# Revit family: Zurn_One-System-Zurn-Z.L6.S
name_source: partatom
category: Plumbing Fixtures
units: mm (PartAtom-declared; Revit-internal decimal feet)

## family parameters
Always vertical = Yes
Cut with Voids When Loaded = No
Maintain Annotation Orientation = No
OmniClass Number = 23.45.05.14
OmniClass Title = Plumbing Fixtures - Sanitary Washing Units
Part Type = Normal
Room Calculation Point = No
Round Connector Dimension = Use Radius
Shared = No
Work Plane-Based = No

## types (1)
- Z.L6.S (20” x 18” Wall Hung Lavatory Zurn One Sensor Hand Washing System)
    Activation Method = Sensor Activation
    Angle stop Location from Sink Top = 10 "
    Assembly Code = D2010
    CW Connection = Yes
    CWFU = 1
    Cold Water Inlet Connection Size (inch) = 0.5 "
    Default Elevation = 0 "
    Description = 20” x 18” Wall Hung Lavatory Zurn One Sensor Hand Washing System
    Distance B/w Angle Stop Body Location = 8 "
    Distance between Sink and Ground = 34 "
    Faucet Material = Chrome-Plated Brass - Zurn - Polished
    Faucet Number = ZG6915-XL
    Fixture Material = China - Zurn - Vitreous
    Fixture Number = Z5344
    Flow Rate (GPM) = 1 GPM
    HW Connection = Yes
    HWFU = 1
    Hot Water Inlet Connection Size (inch) = 0.5 "
    Length odf Sink = 18.25 "
    Manufacturer = Zurn
    Manufacturer Brand = Zurn Water, LLC
    Model = Z.L6.S
    Modified Date = 02/25/2026
    P-trap Hole Location = 12.75 "
    Product Documentation Link = https://files.zurn.com
    Product Page URL = https://www.zurn.com
    Product data URL = https://bimobject.com
    URL = https://www.zurn.com
    Vent Connection = No
    WFU = 1
    Waste Connection = Yes
    Waster water Outlet Connection Size (in) = 0.5 "

## geometry (parser evidence)
native form markers: Blend x36, Sweep x62
no freeform markers — native parametric forms only
